# Revit family: SANINDUSA_107832004_MorairaPlus_ShowerTray120x90_V0
name_source: partatom
category: Plumbing Fixtures
units: mm (PartAtom-declared; Revit-internal decimal feet)

## family parameters
Cut with Voids When Loaded = No
Host = Face
Part Type = Normal
Room Calculation Point = No
Round Connector Dimension = Use Diameter
Shared = No

## types (1)
- SANINDUSA_107832004_MorairaPlus_ShowerTray120x90_V0
    AssetType = Fixed
    CodePerformance = EN 14527:2006 / A1:2010 CL 2
    Color = white
    Constituents = 48711-90 shower tray drain (not included)
    Default Elevation = 1219 mm
    Description = Installation or waste water appliance that emits a spray of water to wash the human body (BS6100)
    DrainSize = 90 mm  [stored 0.295276 ft]
    Element Type = SHOWER: Installation or waste water appliance that emits a spray of water to wash the human body (BS6100)
    Features = Made of ceramic, they are perfectly adaptable to construction from scratch or renovation and are distinguished by their ease and speed of application. The simple design and the simple relief on the surface, allow for integration in both sober and sophisticated projects. With various dimensions, they allow a harmonious setting in smaller or more spacious bathrooms.
    Finish = gloss
    HasTray = TRUE
    Installation Instructions = https://www.tec.sanindusa.pt
    Manufacturer = Sanindusa
    ManufacturerName = Sanindusa
    ManufacturerURL = www.tec.sanindusa.pt
    Material = Fine Fireclay
    Model = 107832004
    ModelNumber = 107832004
    ModelReference = Moraira Plus
    MountingType = AboveTheFloor
    Name = 120x90 Moraira Plus shower tray
    NominalDepth = 67 mm
    NominalHeight = 81 mm  [stored 0.265748 ft]
    NominalLength = 1190 mm  [stored 3.9042 ft]
    NominalWidth = 895 mm  [stored 2.93635 ft]
    Non-slip surface = FALSE
    ProductInformation = https://www.tec.sanindusa.pt
    ProductionYear = 2018
    Shape = rectangular
    ShowerType = Individual
    Size = 120x90
    URL = www.tec.sanindusa.pt
    WarrantyDescription = https://www.tec.sanindusa.pt
    WarrantyDurationParts = 5
    Waste Connection = Yes
    Weight = 44.20 kg

note: [stored X ft] marks values corroborated as IEEE doubles in the binary element streams (Revit-internal decimal feet)

## geometry (parser evidence)
native form markers: Sweep x7
no freeform markers — native parametric forms only
